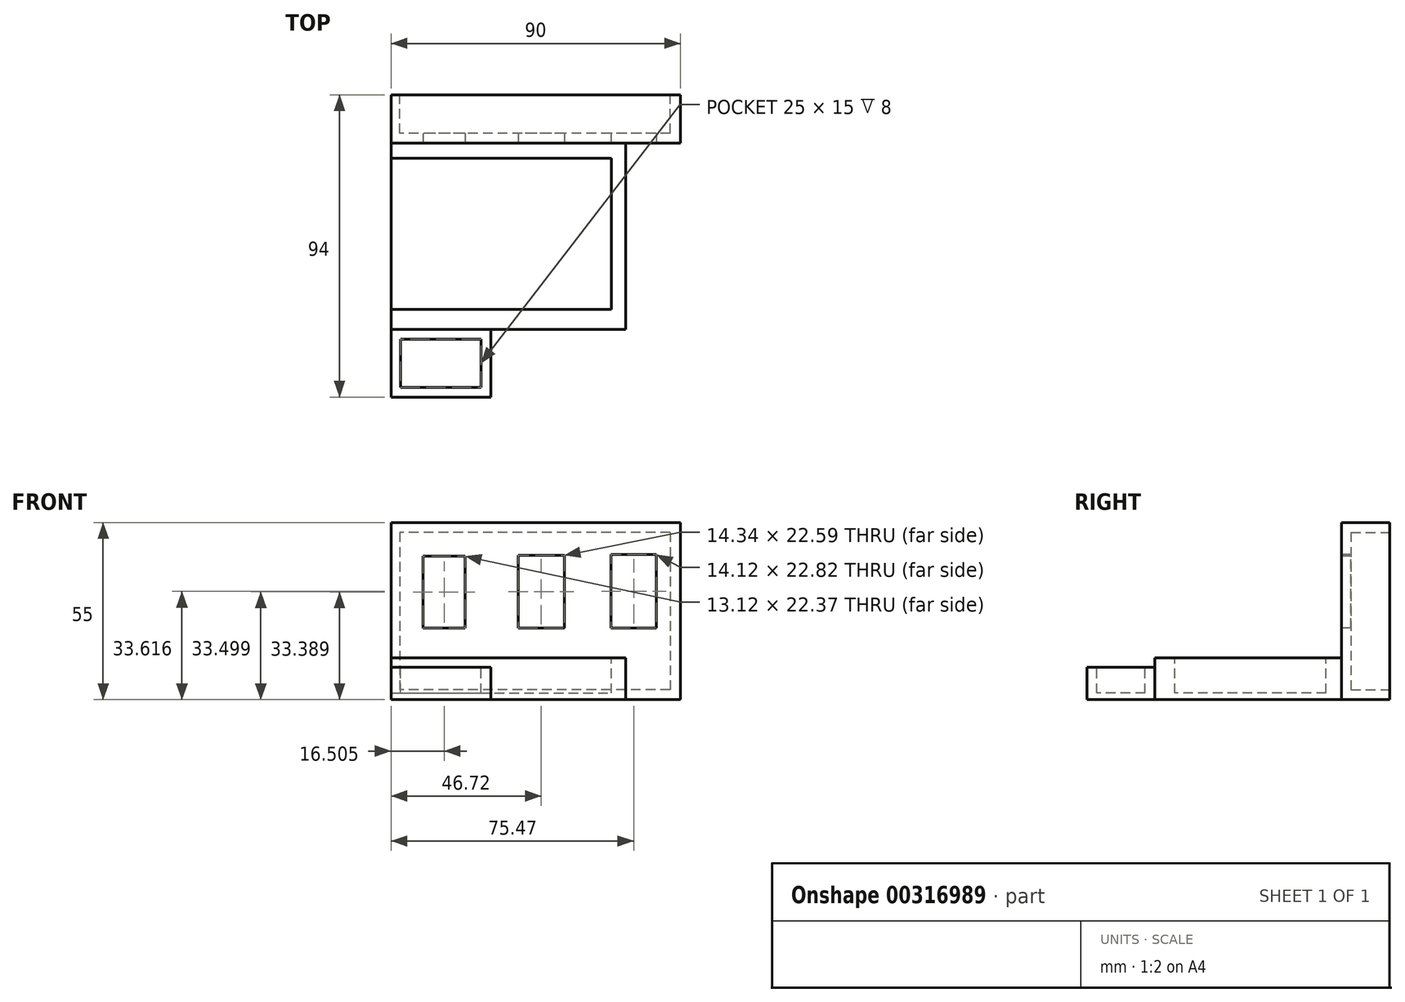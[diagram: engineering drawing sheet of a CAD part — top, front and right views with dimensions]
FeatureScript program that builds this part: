
annotation { "Feature Type Name" : "Feature", "Feature Type Description" : "" }
export const myFeature = defineFeature(function(context is Context, id is Id, definition is map)
    precondition{}
    {
        {
            var Q0;
            Q0=qCreatedBy(makeId("Top.planeOp"),FACE);
            var sketch = newSketch(context, id + "F0", { "sketchPlane" : qUnion([Q0])});
            skLineSegment(sketch, "E0.bottom", {"start": v(0, 0) * mm, "end": v(73, 0) * mm});
            skLineSegment(sketch, "E0.top", {"start": v(0, -58) * mm, "end": v(73, -58) * mm});
            skLineSegment(sketch, "E0.left", {"start": v(0, 0) * mm, "end": v(0, -58) * mm});
            skLineSegment(sketch, "E0.right", {"start": v(73, 0) * mm, "end": v(73, -58) * mm});
            skSolve(sketch);
        }
        {
            var Q0;
            Q0=makeQuery(id+"F0.imprint","IMPRINT",FACE,{"disambiguationData":[TD([[makeQuery(id+"F0.imprint","IMPRINT",EDGE,{"derivedFrom":sQuery(id+"F0.wireOp",EDGE,"E0.bottom")}),-1.0]])]});
            extrude(context, id + "F1", {"entities" : qUnion([Q0]), "depth" : 13 * mm});
        }
        {
            var Q0;
            Q0=makeQuery(id+"F1.opExtrude","CAP_FACE",FACE,{"disambiguationData":[OSD([sQuery(id+"F0.wireOp",EDGE,"E0.bottom"),sQuery(id+"F0.wireOp",EDGE,"E0.top"),sQuery(id+"F0.wireOp",EDGE,"E0.left"),sQuery(id+"F0.wireOp",EDGE,"E0.right")])],"isStart":false});
            var sketch = newSketch(context, id + "F2", { "sketchPlane" : qUnion([Q0])});
            skLineSegment(sketch, "E1.bottom", {"start": v(5.2, -4.73) * mm, "end": v(68.46, -4.73) * mm});
            skLineSegment(sketch, "E1.top", {"start": v(5.2, -51.7) * mm, "end": v(68.46, -51.7) * mm});
            skLineSegment(sketch, "E1.left", {"start": v(5.2, -4.73) * mm, "end": v(5.2, -51.7) * mm});
            skLineSegment(sketch, "E1.right", {"start": v(68.46, -4.73) * mm, "end": v(68.46, -51.7) * mm});
            skSolve(sketch);
        }
        {
            var Q0;
            Q0 = qSketchRegion(id + "F2", true);
            extrude(context, id + "F3", {"entities" : qUnion([Q0]), "operationType" : NewBodyOperationType.REMOVE, "oppositeDirection" : true, "depth" : 11 * mm});
        }
        {
            var Q0;
            Q0=makeQuery(id+"F1.opExtrude","CAP_FACE",FACE,{"disambiguationData":[OSD([sQuery(id+"F0.wireOp",EDGE,"E0.bottom"),sQuery(id+"F0.wireOp",EDGE,"E0.top"),sQuery(id+"F0.wireOp",EDGE,"E0.left"),sQuery(id+"F0.wireOp",EDGE,"E0.right")])],"isStart":false});
            var sketch = newSketch(context, id + "F4", { "sketchPlane" : qUnion([Q0])});
            skLineSegment(sketch, "E2.bottom", {"start": v(5.2, -4.73) * mm, "end": v(0, -4.73) * mm});
            skLineSegment(sketch, "E2.top", {"start": v(5.2, -51.7) * mm, "end": v(0, -51.7) * mm});
            skLineSegment(sketch, "E2.left", {"start": v(5.2, -4.73) * mm, "end": v(5.2, -51.7) * mm});
            skLineSegment(sketch, "E2.right", {"start": v(0, -4.73) * mm, "end": v(0, -51.7) * mm});
            skSolve(sketch);
        }
        {
            var Q0;
            Q0 = qSketchRegion(id + "F4", true);
            extrude(context, id + "F5", {"entities" : qUnion([Q0]), "operationType" : NewBodyOperationType.REMOVE, "oppositeDirection" : true, "depth" : 11 * mm});
        }
        {
            var Q0;
            Q0=qCreatedBy(makeId("Top.planeOp"),FACE);
            var sketch = newSketch(context, id + "F6", { "sketchPlane" : qUnion([Q0])});
            skLineSegment(sketch, "E3.bottom", {"start": v(0, 0) * mm, "end": v(90, 0) * mm});
            skLineSegment(sketch, "E3.top", {"start": v(0, 15) * mm, "end": v(90, 15) * mm});
            skLineSegment(sketch, "E3.left", {"start": v(0, 0) * mm, "end": v(0, 15) * mm});
            skLineSegment(sketch, "E3.right", {"start": v(90, 0) * mm, "end": v(90, 15) * mm});
            skSolve(sketch);
        }
        {
            var Q0;
            Q0=makeQuery(id+"F6.imprint","IMPRINT",FACE,{"disambiguationData":[TD([[makeQuery(id+"F6.imprint","IMPRINT",EDGE,{"derivedFrom":sQuery(id+"F6.wireOp",EDGE,"E3.bottom")}),1.0]])]});
            extrude(context, id + "F7", {"entities" : qUnion([Q0]), "operationType" : NewBodyOperationType.ADD, "depth" : 55 * mm});
        }
        {
            var Q0;
            Q0=makeQuery(id+"F7.opExtrude","SWEPT_FACE",FACE,{"disambiguationData":[OSD([sQuery(id+"F6.wireOp",EDGE,"E3.top")])]});
            var sketch = newSketch(context, id + "F8", { "sketchPlane" : qUnion([Q0])});
            skLineSegment(sketch, "E4.bottom", {"start": v(-86.78, 51.96) * mm, "end": v(-2.7, 51.96) * mm});
            skLineSegment(sketch, "E4.top", {"start": v(-86.78, 3.05) * mm, "end": v(-2.7, 3.05) * mm});
            skLineSegment(sketch, "E4.left", {"start": v(-86.78, 51.96) * mm, "end": v(-86.78, 3.05) * mm});
            skLineSegment(sketch, "E4.right", {"start": v(-2.7, 51.96) * mm, "end": v(-2.7, 3.05) * mm});
            skSolve(sketch);
        }
        {
            var Q0;
            Q0=makeQuery(id+"F8.imprint","IMPRINT",FACE,{"disambiguationData":[TD([[makeQuery(id+"F8.imprint","IMPRINT",EDGE,{"derivedFrom":sQuery(id+"F8.wireOp",EDGE,"E4.bottom")}),-1.0]])]});
            extrude(context, id + "F9", {"entities" : qUnion([Q0]), "operationType" : NewBodyOperationType.REMOVE, "oppositeDirection" : true, "depth" : 12 * mm});
        }
        {
            var Q0;
            Q0=qCreatedBy(makeId("Top.planeOp"),FACE);
            var sketch = newSketch(context, id + "F10", { "sketchPlane" : qUnion([Q0])});
            skLineSegment(sketch, "E5.bottom", {"start": v(0, -58) * mm, "end": v(31, -58) * mm});
            skLineSegment(sketch, "E5.top", {"start": v(0, -79) * mm, "end": v(31, -79) * mm});
            skLineSegment(sketch, "E5.left", {"start": v(0, -58) * mm, "end": v(0, -79) * mm});
            skLineSegment(sketch, "E5.right", {"start": v(31, -58) * mm, "end": v(31, -79) * mm});
            skSolve(sketch);
        }
        {
            var Q0;
            Q0 = qSketchRegion(id + "F10", true);
            extrude(context, id + "F11", {"entities" : qUnion([Q0]), "operationType" : NewBodyOperationType.ADD, "depth" : 10 * mm});
        }
        {
            var Q0;
            Q0=makeQuery(id+"F11.opExtrude","CAP_FACE",FACE,{"disambiguationData":[OSD([sQuery(id+"F10.wireOp",EDGE,"E5.bottom"),sQuery(id+"F10.wireOp",EDGE,"E5.top"),sQuery(id+"F10.wireOp",EDGE,"E5.left"),sQuery(id+"F10.wireOp",EDGE,"E5.right")])],"isStart":false});
            var sketch = newSketch(context, id + "F12", { "sketchPlane" : qUnion([Q0])});
            skLineSegment(sketch, "E6.bottom", {"start": v(3, -61) * mm, "end": v(28, -61) * mm});
            skLineSegment(sketch, "E6.top", {"start": v(3, -76) * mm, "end": v(28, -76) * mm});
            skLineSegment(sketch, "E6.left", {"start": v(3, -61) * mm, "end": v(3, -76) * mm});
            skLineSegment(sketch, "E6.right", {"start": v(28, -61) * mm, "end": v(28, -76) * mm});
            skSolve(sketch);
        }
        {
            var Q0;
            Q0=makeQuery(id+"F12.imprint","IMPRINT",FACE,{"disambiguationData":[TD([[makeQuery(id+"F12.imprint","IMPRINT",EDGE,{"derivedFrom":sQuery(id+"F12.wireOp",EDGE,"E6.bottom")}),-1.0]])]});
            extrude(context, id + "F13", {"entities" : qUnion([Q0]), "operationType" : NewBodyOperationType.REMOVE, "oppositeDirection" : true, "depth" : 8 * mm});
        }
        {
            var Q0;
            Q0=makeQuery(id+"F7.opExtrude","SWEPT_FACE",FACE,{"disambiguationData":[OSD([sQuery(id+"F6.wireOp",EDGE,"E3.bottom")])]});
            var sketch = newSketch(context, id + "F14", { "sketchPlane" : qUnion([Q0])});
            skLineSegment(sketch, "E7.bottom", {"start": v(9.94, 44.57) * mm, "end": v(23.07, 44.57) * mm});
            skLineSegment(sketch, "E7.top", {"start": v(9.94, 22.2) * mm, "end": v(23.07, 22.2) * mm});
            skLineSegment(sketch, "E7.left", {"start": v(9.94, 44.57) * mm, "end": v(9.94, 22.2) * mm});
            skLineSegment(sketch, "E7.right", {"start": v(23.07, 44.57) * mm, "end": v(23.07, 22.2) * mm});
            skLineSegment(sketch, "E8.bottom", {"start": v(39.55, 44.8) * mm, "end": v(53.9, 44.8) * mm});
            skLineSegment(sketch, "E8.top", {"start": v(39.55, 22.2) * mm, "end": v(53.9, 22.2) * mm});
            skLineSegment(sketch, "E8.left", {"start": v(39.55, 44.8) * mm, "end": v(39.55, 22.2) * mm});
            skLineSegment(sketch, "E8.right", {"start": v(53.9, 44.8) * mm, "end": v(53.9, 22.2) * mm});
            skLineSegment(sketch, "E9.bottom", {"start": v(68.41, 45.03) * mm, "end": v(82.53, 45.03) * mm});
            skLineSegment(sketch, "E9.top", {"start": v(68.41, 22.2) * mm, "end": v(82.53, 22.2) * mm});
            skLineSegment(sketch, "E9.left", {"start": v(68.41, 45.03) * mm, "end": v(68.41, 22.2) * mm});
            skLineSegment(sketch, "E9.right", {"start": v(82.53, 45.03) * mm, "end": v(82.53, 22.2) * mm});
            skSolve(sketch);
        }
        {
            var Q0;
            Q0 = qSketchRegion(id + "F14", true);
            extrude(context, id + "F15", {"entities" : qUnion([Q0]), "operationType" : NewBodyOperationType.REMOVE, "oppositeDirection" : true, "depth" : 25 * mm});
        }
    });
